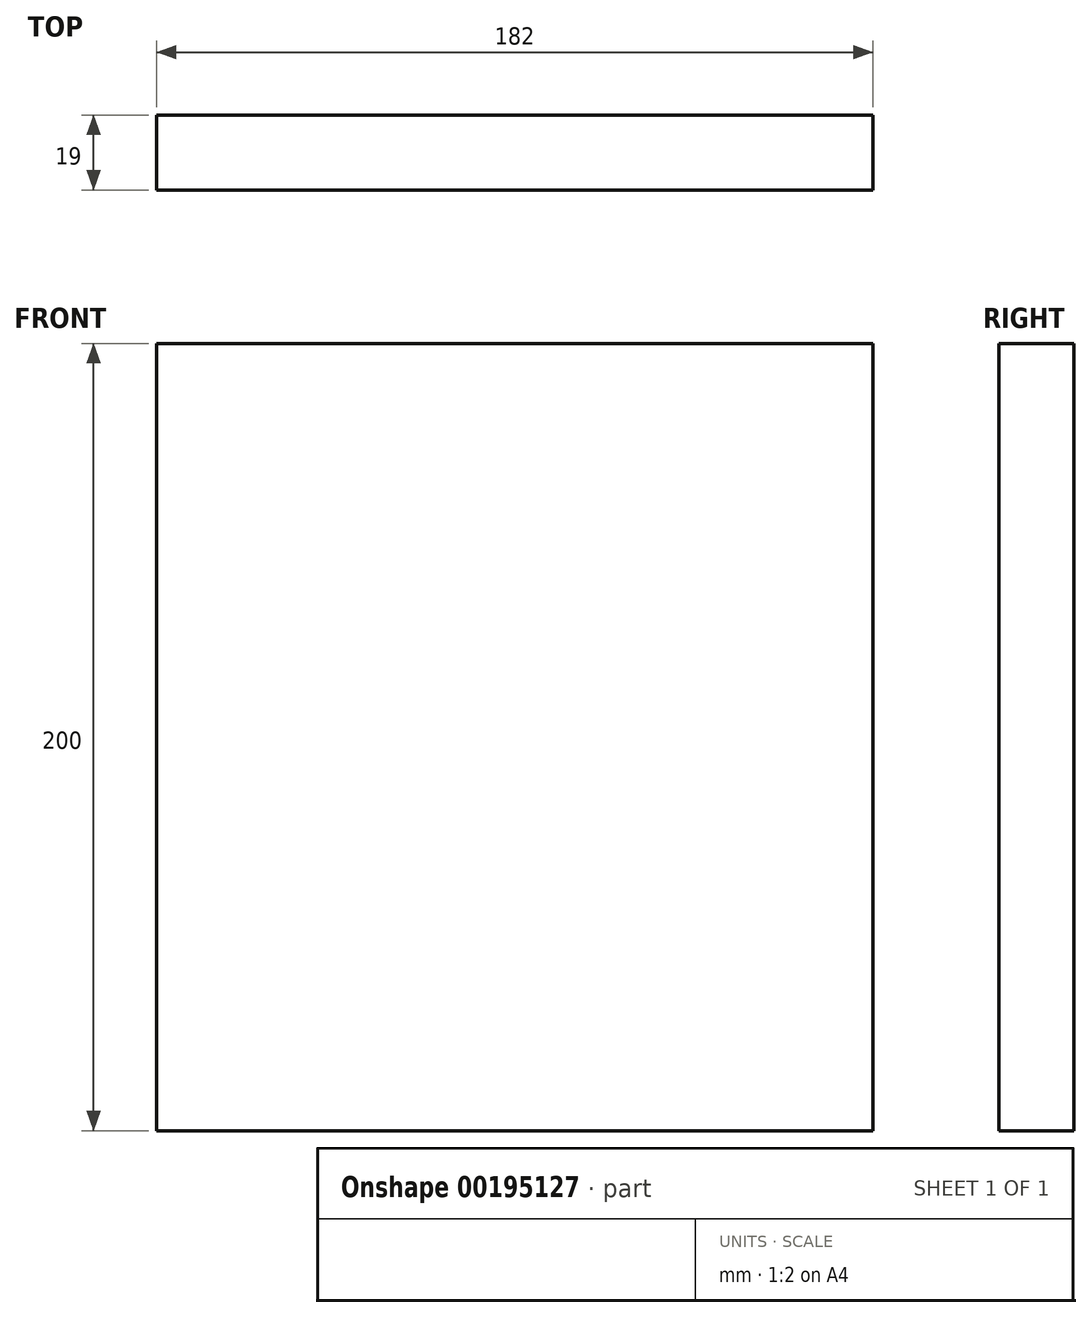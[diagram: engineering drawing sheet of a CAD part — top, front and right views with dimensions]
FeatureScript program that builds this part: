
annotation { "Feature Type Name" : "Feature", "Feature Type Description" : "" }
export const myFeature = defineFeature(function(context is Context, id is Id, definition is map)
    precondition{}
    {
        {
            var Q0;
            Q0=qCreatedBy(makeId("Front.planeOp"),FACE);
            var sketch = newSketch(context, id + "F0", { "sketchPlane" : qUnion([Q0])});
            skLineSegment(sketch, "E0.bottom", {"start": v(-163.63, 282.05) * mm, "end": v(18.37, 282.05) * mm});
            skLineSegment(sketch, "E0.top", {"start": v(-163.63, 82.05) * mm, "end": v(18.37, 82.05) * mm});
            skLineSegment(sketch, "E0.left", {"start": v(-163.63, 282.05) * mm, "end": v(-163.63, 82.05) * mm});
            skLineSegment(sketch, "E0.right", {"start": v(18.37, 282.05) * mm, "end": v(18.37, 82.05) * mm});
            skSolve(sketch);
        }
        {
            var Q0;
            Q0=makeQuery(id+"F0.imprint","IMPRINT",FACE,{"disambiguationData":[TD([[makeQuery(id+"F0.imprint","IMPRINT",EDGE,{"derivedFrom":sQuery(id+"F0.wireOp",EDGE,"E0.bottom")}),-1.0]])]});
            extrude(context, id + "F1", {"entities" : qUnion([Q0]), "depth" : 19 * mm});
        }
    });
